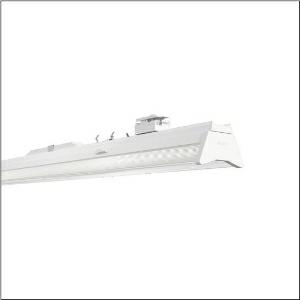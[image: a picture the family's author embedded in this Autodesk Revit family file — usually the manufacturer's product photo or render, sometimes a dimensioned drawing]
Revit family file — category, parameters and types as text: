
# Revit family: licross_21_performance_mo_51td16vnd8xg
name_source: partatom
category: Lighting Fixtures
units: mm (PartAtom-declared; Revit-internal decimal feet)

## family parameters
Cut with Voids When Loaded = No
Host = Face
Light Source = No
Part Type = Normal
Room Calculation Point = No
Round Connector Dimension = Use Diameter
Shared = No

## types (1)
- --- (1 x LED, 8000 lm, 48.3 W, 4000K)
    Apparent Load = 48 VA
    CIE Flux Codes = 66 88 96 79 100
    Color Rendering = 90
    Color Temperature = 4000K
    Default Elevation = 1800 mm
    Description = Licross 21 Performance MO, luminaire insert, of sheet steel, galvanised, coil coated, white, length: 1.500mm, width: 120mm, height: 123mm, LED rated luminous flux: 8.000lm, light colour: 940, SDCM (Standard Deviation of Colour Matching)MacAdam ≤ 2 SDCM (initial), control gear: DALI 2, CLO, with plug, 5-pole, with phase selection, mains connection: 220..240V, AC, 50/60Hz, start of lifetime: 48W, end of service life: 53W, internal wiring halogen-free, primary light control with lens, of plastic, primary optical cover: cover, of PMMA, light emission: direct/indirect distribution, primary light characteristic: symmetric, protection rating (complete): IP54, insulation class (complete): insulation class I (protective earthing), certification: CE, ENEC, VDE, UKCA, protection symbol: D if used in an environment with non-conductive dust loads with corresponding accessories, impact resistance: IK06, permissible ambient temperature for indoor applications: -25..+35°C, corresponds to IFS (International Featured Standards) requirements for safety and quality in the food industry, reducing of maximum allowable ambient temperature of 5°C with ceiling mounting, LABS conformity tested according to VDMA 24364:2018-05, The light source and the operating device comply with the requirements of the Ecodesign Regulation (EU) 2019/2020 and are replaceable in accordance with this regulation, packaging unit: 1 piece
    Height = 114 mm
    Lamp = 1 x LED
    Lamp Light Flux = 8000 lm
    Lamp Power = 48.3 W
    Lamp count = 1
    Length = 1500 mm
    Luminous efficacy = 166 lm/W
    Manufacturer = Siteco
    ModVariant = No
    Model = 51TD16VND8XG
    Mounting Place = Ceiling
    Mounting Type = Pendant
    Number of Poles = 1
    OnlyDefault = Yes
    Power Factor = 1
    Product Name = Licross 21 Performance MO
    Product group = luminaire insert | ceiling pendant
    ProductGroupID = 901
    Protection Class = Protection class I
    Protection Degree = IP 54
    RLX_Detail_Level = 1
    RLX_Emergency_Light_Flux = 0 lm
    RLX_Emergency_Type = 0
    RLX_Emergency_Type_DB = No
    RlxData = <blob elided: 34425 chars, md5=6e5d7cda>
    Socket = socket
    Standby Power = 0 W
    System Light Flux = 8000 lm
    System Power = 48 W
    Type Comments = factory setting: luminous flux: 100 % | dim-lin: 254 | 324 mA
    Type Image = l_1256138.jpg
    URL = http://relux.com
    VarID = @adj_093119
    Voltage = 0 V
    Weight = 0.00 kg
    Width = 120 mm

## geometry (parser evidence)
native form markers: Blend x4, Sweep x11
no freeform markers — native parametric forms only
